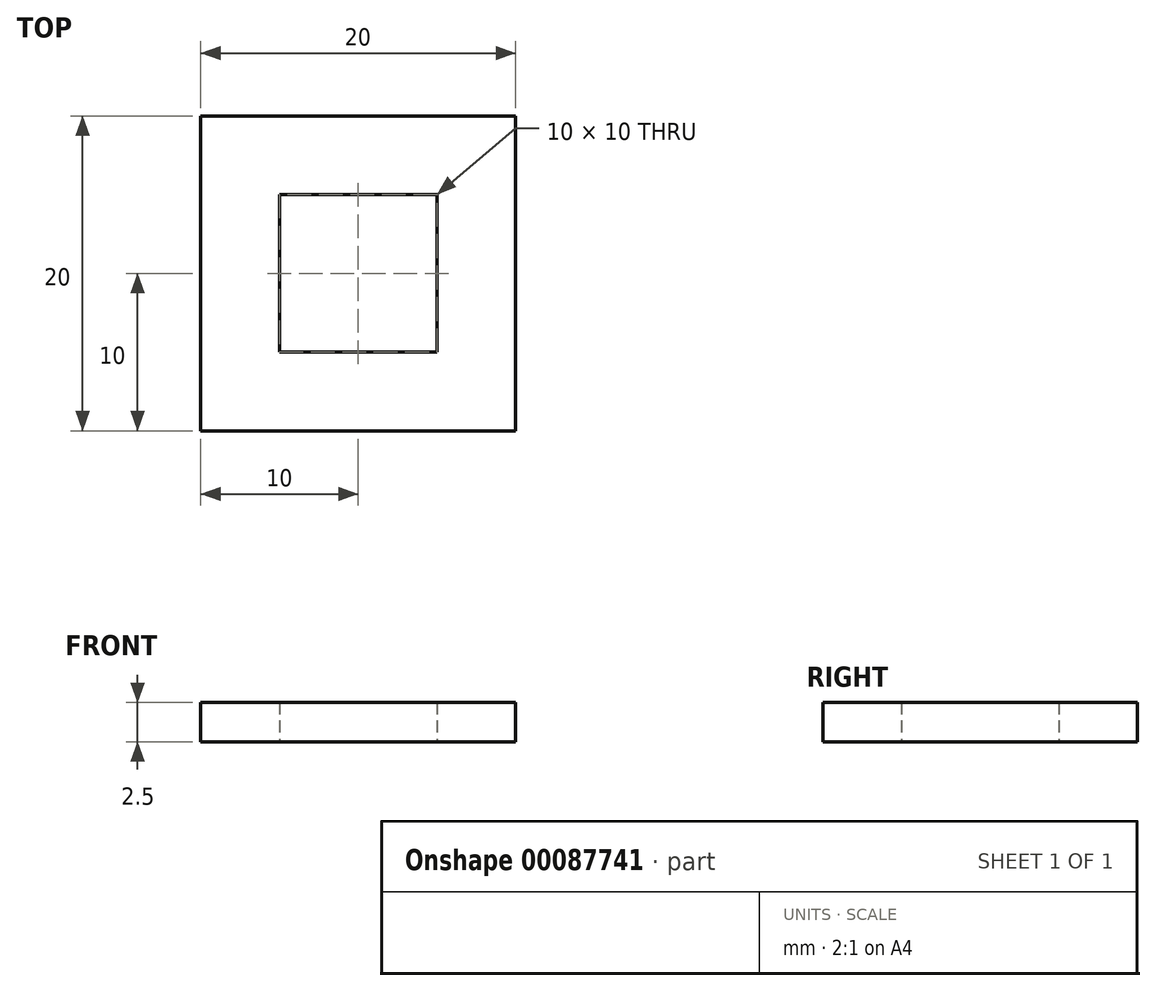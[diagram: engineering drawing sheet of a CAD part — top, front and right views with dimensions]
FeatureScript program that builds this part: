
annotation { "Feature Type Name" : "Feature", "Feature Type Description" : "" }
export const myFeature = defineFeature(function(context is Context, id is Id, definition is map)
    precondition{}
    {
        {
            var Q0;
            Q0=qCreatedBy(makeId("Front.planeOp"),FACE);
            var sketch = newSketch(context, id + "F0", { "sketchPlane" : qUnion([Q0])});
            skLineSegment(sketch, "E0.bottom", {"start": v(5, -5) * mm, "end": v(-5, -5) * mm});
            skLineSegment(sketch, "E0.top", {"start": v(5, 5) * mm, "end": v(-5, 5) * mm});
            skLineSegment(sketch, "E0.left", {"start": v(5, -5) * mm, "end": v(5, 5) * mm});
            skLineSegment(sketch, "E0.right", {"start": v(-5, -5) * mm, "end": v(-5, 5) * mm});
            skPoint(sketch, "E0.middle", {"position": v(0, 0) * mm});
            skLineSegment(sketch, "E1.0", {"start": v(-10, -10) * mm, "end": v(-10, 10) * mm});
            skLineSegment(sketch, "E1.1", {"start": v(10, -10) * mm, "end": v(-10, -10) * mm});
            skLineSegment(sketch, "E1.2", {"start": v(10, -10) * mm, "end": v(10, 10) * mm});
            skLineSegment(sketch, "E1.3", {"start": v(10, 10) * mm, "end": v(-10, 10) * mm});
            skLineSegment(sketch, "E2.0", {"start": v(-25, -25) * mm, "end": v(-25, 25) * mm});
            skLineSegment(sketch, "E2.1", {"start": v(25, -25) * mm, "end": v(-25, -25) * mm});
            skLineSegment(sketch, "E2.2", {"start": v(25, -25) * mm, "end": v(25, 25) * mm});
            skLineSegment(sketch, "E2.3", {"start": v(25, 25) * mm, "end": v(-25, 25) * mm});
            skLineSegment(sketch, "E3.0", {"start": v(-30, -30) * mm, "end": v(-30, 30) * mm});
            skLineSegment(sketch, "E3.1", {"start": v(30, -30) * mm, "end": v(-30, -30) * mm});
            skLineSegment(sketch, "E3.2", {"start": v(30, -30) * mm, "end": v(30, 30) * mm});
            skLineSegment(sketch, "E3.3", {"start": v(30, 30) * mm, "end": v(-30, 30) * mm});
            skSolve(sketch);
        }
        {
            var Q0;
            Q0=makeQuery(id+"F0.imprint","IMPRINT",FACE,{"disambiguationData":[TD([[makeQuery(id+"F0.imprint","IMPRINT",EDGE,{"derivedFrom":sQuery(id+"F0.wireOp",EDGE,"E0.bottom")}),1.0]])]});
            extrude(context, id + "F1", {"entities" : qUnion([Q0]), "depth" : 2.5 * mm});
        }
        {
            var Q0;
            Q0=makeQuery(id+"F1.opExtrude","SWEPT_BODY",BODY,{"disambiguationData":[OSD([sQuery(id+"F0.wireOp",EDGE,"E0.bottom"),sQuery(id+"F0.wireOp",EDGE,"E0.top"),sQuery(id+"F0.wireOp",EDGE,"E0.left"),sQuery(id+"F0.wireOp",EDGE,"E0.right"),sQuery(id+"F0.wireOp",EDGE,"E1.0"),sQuery(id+"F0.wireOp",EDGE,"E1.1"),sQuery(id+"F0.wireOp",EDGE,"E1.2"),sQuery(id+"F0.wireOp",EDGE,"E1.3")])]});
            var Q1;
            Q1=makeQuery(id+"F1.opExtrude","CAP_EDGE",EDGE,{"disambiguationData":[OSD([sQuery(id+"F0.wireOp",EDGE,"E1.3")])],"isStart":false});
            transform(context, id + "F2", {"entities" : qUnion([Q0]), "transformType" : TransformType.ROTATION, "transformAxis" : qUnion([Q1]), "angle" : 90 * degree, "makeCopy" : false});
        }
    });
